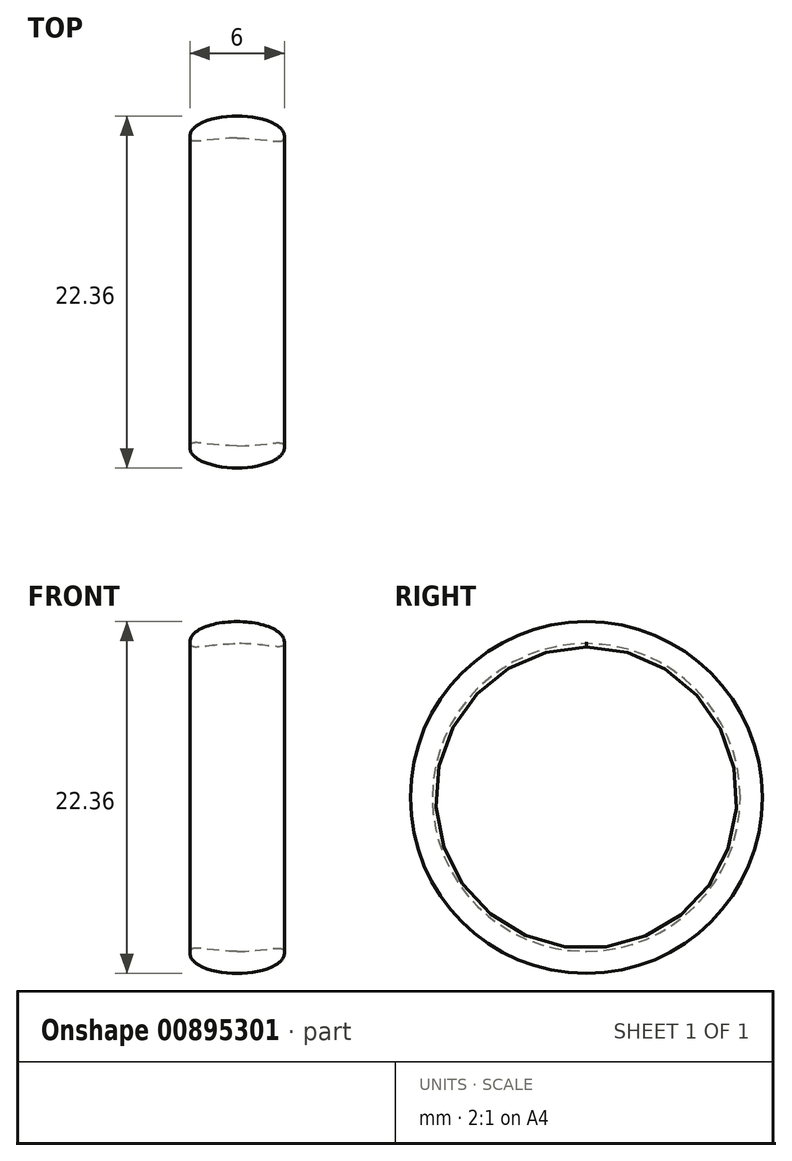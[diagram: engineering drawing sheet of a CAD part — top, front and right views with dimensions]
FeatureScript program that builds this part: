
annotation { "Feature Type Name" : "Feature", "Feature Type Description" : "" }
export const myFeature = defineFeature(function(context is Context, id is Id, definition is map)
    precondition{}
    {
        {
            var Q0;
            Q0=qCreatedBy(makeId("Top.planeOp"),FACE);
            var sketch = newSketch(context, id + "F0", { "sketchPlane" : qUnion([Q0])});
            skLineSegment(sketch, "E0", {"start": v(0, 0) * mm, "end": v(4.65, 0) * mm, "construction": true});
            skFitSpline(sketch, "E1", {"points": [v(0, 11.18) * mm, v(-3, 9.88) * mm], "startDerivative": vector(-4.5, 0) * mm, "endDerivative": vector(0, -2.4) * mm});
            skFitSpline(sketch, "E2", {"points": [v(-3, 9.88) * mm, v(0, 9.78) * mm], "startDerivative": vector(0, -1.83) * mm, "endDerivative": vector(6.35, 0) * mm});
            skLineSegment(sketch, "E3", {"start": v(-6.07, 9.57) * mm, "end": v(-3.23, 9.57) * mm, "construction": true});
            skLineSegment(sketch, "E4.MirrorCS", {"start": v(6.07, 9.57) * mm, "end": v(3.23, 9.57) * mm, "construction": true});
            skFitSpline(sketch, "E5.MirrorCS", {"points": [v(0, 11.18) * mm, v(3, 9.88) * mm], "startDerivative": vector(4.5, 0) * mm, "endDerivative": vector(0, -2.4) * mm});
            skFitSpline(sketch, "E6.MirrorCS", {"points": [v(3, 9.88) * mm, v(0, 9.78) * mm], "startDerivative": vector(0, -1.83) * mm, "endDerivative": vector(-6.35, 0) * mm});
            skSolve(sketch);
        }
        {
            var Q0;
            Q0=makeQuery(id+"F0.imprint","IMPRINT",FACE,{"disambiguationData":[TD([[makeQuery(id+"F0.imprint","IMPRINT",EDGE,{"derivedFrom":sQuery(id+"F0.wireOp",EDGE,"E1")}),1.0]])]});
            var Q1;
            Q1=sQuery(id+"F0.wireOp",EDGE,"E0");
            revolve(context, id + "F1", {"surfaceOperationType" : NewSurfaceOperationType.NEW, "entities" : qUnion([Q0]), "axis" : qUnion([Q1]), "revolveType" : RevolveType.FULL});
        }
    });
